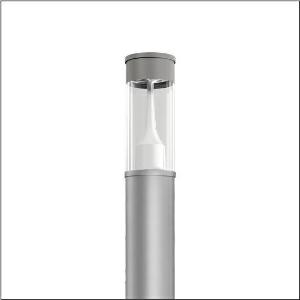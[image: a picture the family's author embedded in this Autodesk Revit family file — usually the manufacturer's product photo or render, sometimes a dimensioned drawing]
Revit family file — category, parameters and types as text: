
# Revit family: city-light_260_iq___pl1_2s_5xa5295rf14h_a018
name_source: partatom
category: Lighting Fixtures
units: mm (PartAtom-declared; Revit-internal decimal feet)

## family parameters
Cut with Voids When Loaded = No
Host = Face
Light Source = No
Part Type = Normal
Room Calculation Point = No
Round Connector Dimension = Use Diameter
Shared = No

## types (1)
- --- (1 x LED, 2970 lm, 18.5 W, 4000K)
    Apparent Load = 19 VA
    CIE Flux Codes = 23 62 94 96 100
    Color Rendering = 70
    Color Temperature = 4000K
    Default Elevation = 1800 mm
    Description = City-Light 260 iQ, light pillar, Module 540 iQ-SR, primary light control with 3 zone facetted reflector, of plastic, silver coated, highly specular, structured, primary optical cover: cover, of PMMA, transparent, partly coated, light distribution: PL1.2s, primary light characteristic: symmetric, LED, High Power LED, rated luminous flux: 2.970lm, luminous efficacy: 161lm/W, light colour: 740, colour temperature: 4000K, control gear: ECG iQ, control: presetting dimming logarithmic, Street-Remote, Auto-Match, Temp-Guard, Lumen-Switch, Night-Set, Smart-Wire, Light-Fading, Desk-Remote (wireless, voltage-free reading and setting of iQ features in the workshop via application-optimized NFC function/RFID function), optimised constant luminous flux control (CLO 2.0), with terminal, 6-pole, max. 2.5mm², mains connection: 230..240V, AC, 50/60Hz, start of lifetime: 19W, end of service life: 20W, reduction: 9W, luminaire housing, cylindrical, of extruded aluminium section, coated, Siteco® metallic grey (DB 702S), length: 2.600mm, diameter: 200mm, Module 540 iQ-SR, traffic white (RAL 9016), equipment: standard, protection rating (complete): IP65, insulation class (complete): insulation class II (safety insulation), certification: CE, ENEC, VDE, packaging unit: 1 piece

Light Distribution: PL1.2s
    Height = 500 mm
    Lamp = 1 x LED
    Lamp Light Flux = 2970 lm
    Lamp Power = 18.5 W
    Lamp count = 1
    Length = 200 mm  [stored 0.656168 ft]
    Luminous efficacy = 161 lm/W
    Manufacturer = Siteco
    ModVariant = No
    Model = 5XA5295RF14H
    Mounting Place = Floor
    Mounting Type = Freestanding
    Number of Poles = 1
    OnlyDefault = Yes
    Power Factor = 1
    Product Name = City-Light 260 iQ | PL1.2s
    Product group = light pillar
    ProductGroupID = 1303
    Protection Class = Protection class II
    Protection Degree = IP 65
    RLX_Detail_Level = 1
    RLX_Emergency_Light_Flux = 0 lm
    RLX_Emergency_Type = 0
    RLX_Emergency_Type_DB = No
    RlxData = <blob elided: 28829 chars, md5=fc71b44e>
    Socket = socket
    Standby Power = 0 W
    System Light Flux = 2970 lm
    System Power = 19 W
    Type Comments = factory setting: luminous flux: 100 % | dim-lin: 254 | 385 mA
    Type Image = l_1006920.jpg
    URL = http://relux.com
    VarID = @adj_076631
    Voltage = 0 V
    Weight = 0.00 kg
    Width = 0 mm  [stored 0 ft]

note: [stored X ft] marks values corroborated as IEEE doubles in the binary element streams (Revit-internal decimal feet)

## geometry (parser evidence)
native form markers: Blend x4, Sweep x9
no freeform markers — native parametric forms only
